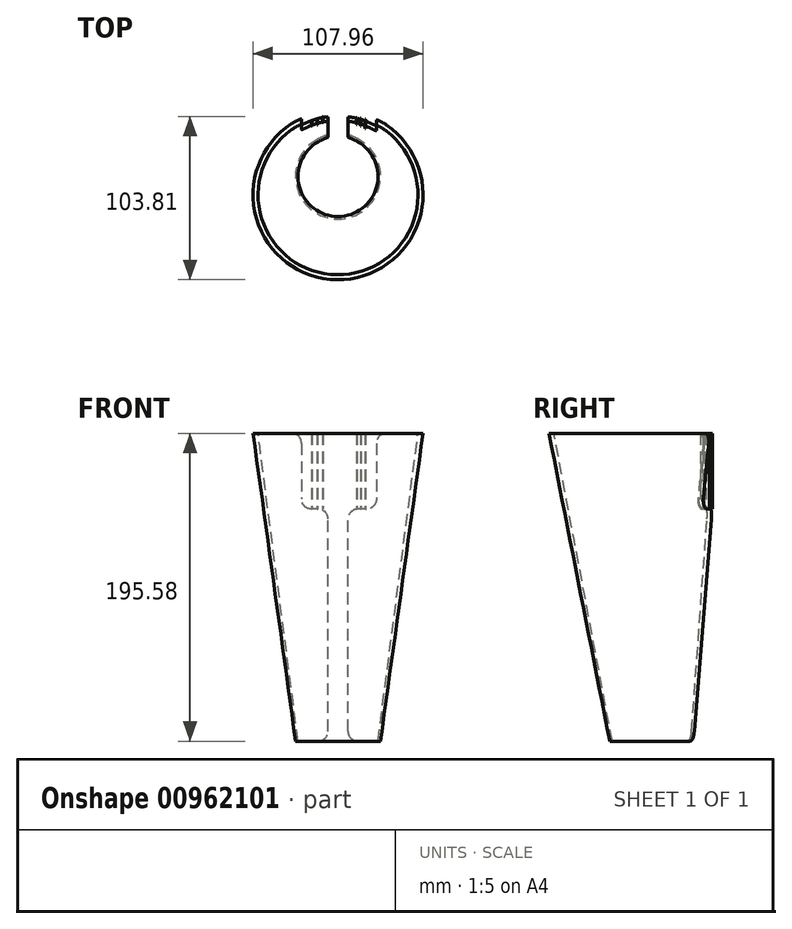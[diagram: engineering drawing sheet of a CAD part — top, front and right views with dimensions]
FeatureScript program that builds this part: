
annotation { "Feature Type Name" : "Feature", "Feature Type Description" : "" }
export const myFeature = defineFeature(function(context is Context, id is Id, definition is map)
    precondition{}
    {
        {
            var Q0;
            Q0=qCreatedBy(makeId("Top.planeOp"),FACE);
            cPlane(context, id + "F0", {"entities" : qUnion([Q0]), "cplaneType" : CPlaneType.OFFSET, "offset" : 195.58 * mm, "width" : 152.4 * mm, "height" : 152.4 * mm});
        }
        {
            var Q0;
            Q0=qCreatedBy(makeId("Top.planeOp"),FACE);
            var sketch = newSketch(context, id + "F1", { "sketchPlane" : qUnion([Q0])});
            skArc(sketch, "E0", {"start": v(-6.35, 24.6) * mm, "mid": v(0, -25.4) * mm, "end": v(6.35, 24.6) * mm});
            skArc(sketch, "E1.0", {"start": v(-6.35, 26.23) * mm, "mid": v(0, -26.99) * mm, "end": v(6.35, 26.23) * mm});
            skLineSegment(sketch, "E2", {"start": v(-6.35, 26.23) * mm, "end": v(-6.35, 24.6) * mm});
            skLineSegment(sketch, "E3", {"start": v(6.35, 26.23) * mm, "end": v(6.35, 24.6) * mm});
            skSolve(sketch);
        }
        {
            var Q0;
            Q0=qCreatedBy(id+"F0.planeOp",FACE);
            var sketch = newSketch(context, id + "F2", { "sketchPlane" : qUnion([Q0])});
            skArc(sketch, "E4", {"start": v(-6.35, 38.8) * mm, "mid": v(0, -62.4) * mm, "end": v(6.35, 38.8) * mm});
            skArc(sketch, "E5.0", {"start": v(-6.35, 42) * mm, "mid": v(0, -65.58) * mm, "end": v(6.35, 42) * mm});
            skLineSegment(sketch, "E6", {"start": v(-6.35, 42) * mm, "end": v(-6.35, 38.8) * mm});
            skLineSegment(sketch, "E7", {"start": v(6.35, 42) * mm, "end": v(6.35, 38.8) * mm});
            skSolve(sketch);
        }
        {
            var Q0;
            Q0=qSketchRegion(id+"F1",true);
            var Q1;
            Q1=qSketchRegion(id+"F2",true);
            loft(context, id + "F3", {"sheetProfilesArray" : [{ "sheetProfileEntities" : qUnion([Q0]) }, { "sheetProfileEntities" : qUnion([Q1]) }]});
        }
        {
            var Q0;
            Q0=qCreatedBy(makeId("Front.planeOp"),FACE);
            var sketch = newSketch(context, id + "F4", { "sketchPlane" : qUnion([Q0])});
            skLineSegment(sketch, "E8.bottom", {"start": v(-23.22, 213.25) * mm, "end": v(24.43, 213.25) * mm});
            skLineSegment(sketch, "E8.top", {"start": v(-23.22, 147.46) * mm, "end": v(24.43, 147.46) * mm});
            skLineSegment(sketch, "E8.left", {"start": v(-23.22, 213.25) * mm, "end": v(-23.22, 147.46) * mm});
            skLineSegment(sketch, "E8.right", {"start": v(24.43, 213.25) * mm, "end": v(24.43, 147.46) * mm});
            skSolve(sketch);
        }
        {
            var Q0;
            Q0=makeQuery(id+"F4.imprint","IMPRINT",FACE,{"disambiguationData":[TD([[makeQuery(id+"F4.imprint","IMPRINT",EDGE,{"derivedFrom":sQuery(id+"F4.wireOp",EDGE,"E8.bottom")}),-1.0]])]});
            extrude(context, id + "F5", {"entities" : qUnion([Q0]), "operationType" : NewBodyOperationType.REMOVE, "oppositeDirection" : true, "depth" : 508 * mm, "offsetDistance" : 25.4 * mm});
        }
        {
            var Q0;
            Q0=makeQuery(id+"F5.boolean.opBoolean","INTERSECT",EDGE,{"derivedFrom":[makeQuery(id+"F3.opLoft","CAP_FACE",FACE,{"disambiguationData":[OSD([makeQuery(id+"F2.imprint","IMPRINT",FACE,{"disambiguationData":[TD([[makeQuery(id+"F2.imprint","IMPRINT",EDGE,{"derivedFrom":sQuery(id+"F2.wireOp",EDGE,"E4")}),-1.0]])]})])],"isStart":true}),makeQuery(id+"F5.opExtrude","SWEPT_FACE",FACE,{"disambiguationData":[OSD([sQuery(id+"F4.wireOp",EDGE,"E8.right")])]})]});
            var Q1;
            Q1=makeQuery(id+"F5.boolean.opBoolean","COPY",EDGE,{"derivedFrom":makeQuery(id+"F5.opExtrude","SWEPT_EDGE",EDGE,{"disambiguationData":[OSD([sQuery(id+"F4.wireOp",EDGE,"E8.top"),sQuery(id+"F4.wireOp",EDGE,"E8.right")])]})});
            var Q2;
            Q2=makeQuery(id+"F5.boolean.opBoolean","INTERSECT",EDGE,{"derivedFrom":[makeQuery(id+"F3.opLoft","SWEPT_FACE",FACE,{"disambiguationData":[OSD([sQuery(id+"F1.wireOp",EDGE,"E0"),sQuery(id+"F1.wireOp",EDGE,"E1.0"),sQuery(id+"F1.wireOp",EDGE,"E3"),sQuery(id+"F2.wireOp",EDGE,"E4"),sQuery(id+"F2.wireOp",EDGE,"E5.0"),sQuery(id+"F2.wireOp",EDGE,"E7")])]}),makeQuery(id+"F5.opExtrude","SWEPT_FACE",FACE,{"disambiguationData":[OSD([sQuery(id+"F4.wireOp",EDGE,"E8.top")])]})]});
            var Q3;
            Q3=makeQuery(id+"F5.boolean.opBoolean","INTERSECT",EDGE,{"derivedFrom":[makeQuery(id+"F3.opLoft","SWEPT_FACE",FACE,{"disambiguationData":[OSD([sQuery(id+"F1.wireOp",EDGE,"E0"),sQuery(id+"F1.wireOp",EDGE,"E1.0"),sQuery(id+"F1.wireOp",EDGE,"E2"),sQuery(id+"F2.wireOp",EDGE,"E4"),sQuery(id+"F2.wireOp",EDGE,"E5.0"),sQuery(id+"F2.wireOp",EDGE,"E6")])]}),makeQuery(id+"F5.opExtrude","SWEPT_FACE",FACE,{"disambiguationData":[OSD([sQuery(id+"F4.wireOp",EDGE,"E8.top")])]})]});
            var Q4;
            Q4=makeQuery(id+"F5.boolean.opBoolean","COPY",EDGE,{"derivedFrom":makeQuery(id+"F5.opExtrude","SWEPT_EDGE",EDGE,{"disambiguationData":[OSD([sQuery(id+"F4.wireOp",EDGE,"E8.top"),sQuery(id+"F4.wireOp",EDGE,"E8.left")])]})});
            var Q5;
            Q5=makeQuery(id+"F5.boolean.opBoolean","INTERSECT",EDGE,{"derivedFrom":[makeQuery(id+"F3.opLoft","CAP_FACE",FACE,{"disambiguationData":[OSD([makeQuery(id+"F2.imprint","IMPRINT",FACE,{"disambiguationData":[TD([[makeQuery(id+"F2.imprint","IMPRINT",EDGE,{"derivedFrom":sQuery(id+"F2.wireOp",EDGE,"E4")}),-1.0]])]})])],"isStart":true}),makeQuery(id+"F5.opExtrude","SWEPT_FACE",FACE,{"disambiguationData":[OSD([sQuery(id+"F4.wireOp",EDGE,"E8.left")])]})]});
            var Q6;
            Q6=makeQuery(id+"F3.opLoft","MID_CAP_EDGE",EDGE,{"disambiguationData":[OSD([sQuery(id+"F1.wireOp",EDGE,"E0"),sQuery(id+"F1.wireOp",EDGE,"E1.0"),sQuery(id+"F1.wireOp",EDGE,"E3")])],"capPos":0.0});
            var Q7;
            Q7=makeQuery(id+"F3.opLoft","MID_CAP_EDGE",EDGE,{"disambiguationData":[OSD([sQuery(id+"F1.wireOp",EDGE,"E0"),sQuery(id+"F1.wireOp",EDGE,"E1.0"),sQuery(id+"F1.wireOp",EDGE,"E2")])],"capPos":0.0});
            fillet(context, id + "F6", {"entities" : qUnion([Q0, Q1, Q2, Q3, Q4, Q5, Q6, Q7]), "radius" : 6.35 * mm, "tangentPropagation" : true, "allowEdgeOverflow" : false});
        }
        {
            var Q0;
            {var subQ0=sQuery(id+"F2.wireOp",EDGE,"E7");var subQ1=sQuery(id+"F2.wireOp",EDGE,"E6");var subQ2=sQuery(id+"F2.wireOp",EDGE,"E4");var subQ3=sQuery(id+"F1.wireOp",EDGE,"E3");var subQ4=sQuery(id+"F1.wireOp",EDGE,"E2");var subQ5=sQuery(id+"F1.wireOp",EDGE,"E0");var subQ6=sQuery(id+"F2.wireOp",EDGE,"E5.0");var subQ7=sQuery(id+"F1.wireOp",EDGE,"E1.0");var subQ8=makeQuery(id+"F3.opLoft","SWEPT_FACE",FACE,{"disambiguationData":[OSD([subQ5,subQ7,subQ4,subQ2,subQ6,subQ1])]});var subQ9=makeQuery(id+"F3.opLoft","SWEPT_FACE",FACE,{"disambiguationData":[OSD([subQ7,subQ4,subQ3,subQ6,subQ1,subQ0])]});var subQ10=makeQuery(id+"F5.opExtrude","SWEPT_FACE",FACE,{"disambiguationData":[OSD([sQuery(id+"F4.wireOp",EDGE,"E8.top")])]});Q0=makeQuery(id+"F6.opFillet","BLEND_VERTEX",VERTEX,{"blendedFrom":[makeQuery(id+"F5.boolean.opBoolean","INTERSECT",EDGE,{"derivedFrom":[subQ8,subQ10]}),subQ9,makeQuery(id+"F5.boolean.opBoolean","COPY",FACE,{"disambiguationData":[TD([makeQuery(id+"F5.opExtrude","SWEPT_FACE",FACE,{"disambiguationData":[OSD([sQuery(id+"F4.wireOp",EDGE,"E8.left")])]})])],"derivedFrom":subQ10})],"blendedInto":[subQ9,makeQuery(id+"F5.boolean.opBoolean","COPY",FACE,{"disambiguationData":[TD([makeQuery(id+"F5.opExtrude","SWEPT_FACE",FACE,{"disambiguationData":[OSD([sQuery(id+"F4.wireOp",EDGE,"E8.left")])]})])],"derivedFrom":subQ10})]});}
            var Q1;
            {var subQ0=sQuery(id+"F2.wireOp",EDGE,"E7");var subQ1=sQuery(id+"F2.wireOp",EDGE,"E6");var subQ2=sQuery(id+"F2.wireOp",EDGE,"E4");var subQ3=sQuery(id+"F1.wireOp",EDGE,"E3");var subQ4=sQuery(id+"F1.wireOp",EDGE,"E2");var subQ5=sQuery(id+"F1.wireOp",EDGE,"E0");var subQ6=makeQuery(id+"F3.opLoft","SWEPT_FACE",FACE,{"disambiguationData":[OSD([subQ5,subQ4,subQ3,subQ2,subQ1,subQ0])]});var subQ7=sQuery(id+"F2.wireOp",EDGE,"E5.0");var subQ8=sQuery(id+"F1.wireOp",EDGE,"E1.0");var subQ9=makeQuery(id+"F3.opLoft","SWEPT_FACE",FACE,{"disambiguationData":[OSD([subQ5,subQ8,subQ4,subQ2,subQ7,subQ1])]});var subQ10=makeQuery(id+"F5.opExtrude","SWEPT_FACE",FACE,{"disambiguationData":[OSD([sQuery(id+"F4.wireOp",EDGE,"E8.top")])]});Q1=makeQuery(id+"F6.opFillet","BLEND_VERTEX",VERTEX,{"blendedFrom":[makeQuery(id+"F5.boolean.opBoolean","INTERSECT",EDGE,{"derivedFrom":[subQ9,subQ10]}),subQ6,makeQuery(id+"F5.boolean.opBoolean","COPY",FACE,{"disambiguationData":[TD([makeQuery(id+"F5.opExtrude","SWEPT_FACE",FACE,{"disambiguationData":[OSD([sQuery(id+"F4.wireOp",EDGE,"E8.left")])]})])],"derivedFrom":subQ10})],"blendedInto":[subQ6,makeQuery(id+"F5.boolean.opBoolean","COPY",FACE,{"disambiguationData":[TD([makeQuery(id+"F5.opExtrude","SWEPT_FACE",FACE,{"disambiguationData":[OSD([sQuery(id+"F4.wireOp",EDGE,"E8.left")])]})])],"derivedFrom":subQ10})]});}
            var Q2;
            {var subQ0=sQuery(id+"F2.wireOp",EDGE,"E7");var subQ1=sQuery(id+"F2.wireOp",EDGE,"E6");var subQ2=sQuery(id+"F2.wireOp",EDGE,"E4");var subQ3=sQuery(id+"F1.wireOp",EDGE,"E3");var subQ4=sQuery(id+"F1.wireOp",EDGE,"E2");var subQ5=sQuery(id+"F1.wireOp",EDGE,"E0");var subQ6=sQuery(id+"F2.wireOp",EDGE,"E5.0");var subQ7=sQuery(id+"F1.wireOp",EDGE,"E1.0");var subQ8=makeQuery(id+"F3.opLoft","SWEPT_FACE",FACE,{"disambiguationData":[OSD([subQ5,subQ7,subQ3,subQ2,subQ6,subQ0])]});var subQ9=makeQuery(id+"F3.opLoft","SWEPT_FACE",FACE,{"disambiguationData":[OSD([subQ7,subQ4,subQ3,subQ6,subQ1,subQ0])]});var subQ10=makeQuery(id+"F5.opExtrude","SWEPT_FACE",FACE,{"disambiguationData":[OSD([sQuery(id+"F4.wireOp",EDGE,"E8.top")])]});Q2=makeQuery(id+"F6.opFillet","BLEND_VERTEX",VERTEX,{"blendedFrom":[makeQuery(id+"F5.boolean.opBoolean","INTERSECT",EDGE,{"derivedFrom":[subQ8,subQ10]}),subQ9,makeQuery(id+"F5.boolean.opBoolean","COPY",FACE,{"disambiguationData":[TD([makeQuery(id+"F5.opExtrude","SWEPT_FACE",FACE,{"disambiguationData":[OSD([sQuery(id+"F4.wireOp",EDGE,"E8.right")])]})])],"derivedFrom":subQ10})],"blendedInto":[subQ9,makeQuery(id+"F5.boolean.opBoolean","COPY",FACE,{"disambiguationData":[TD([makeQuery(id+"F5.opExtrude","SWEPT_FACE",FACE,{"disambiguationData":[OSD([sQuery(id+"F4.wireOp",EDGE,"E8.right")])]})])],"derivedFrom":subQ10})]});}
            cPlane(context, id + "F7", {"entities" : qUnion([Q0, Q1, Q2]), "cplaneType" : CPlaneType.THREE_POINT, "offset" : 25.4 * mm, "width" : 152.4 * mm, "height" : 152.4 * mm});
        }
        {
            var Q0;
            Q0=qCreatedBy(id+"F7.planeOp",FACE);
            var sketch = newSketch(context, id + "F8", { "sketchPlane" : qUnion([Q0])});
            skLineSegment(sketch, "E9.bottom", {"start": v(-16.94, -35.6) * mm, "end": v(-16.66, -35.6) * mm});
            skLineSegment(sketch, "E9.top", {"start": v(-16.94, -32.12) * mm, "end": v(-16.66, -32.12) * mm});
            skLineSegment(sketch, "E9.left", {"start": v(-16.94, -35.6) * mm, "end": v(-16.94, -32.12) * mm});
            skLineSegment(sketch, "E9.right", {"start": v(-16.66, -35.6) * mm, "end": v(-16.66, -32.12) * mm});
            skLineSegment(sketch, "E10.bottom", {"start": v(-13.28, -36.94) * mm, "end": v(-12.87, -36.94) * mm});
            skLineSegment(sketch, "E10.top", {"start": v(-13.28, -32.7) * mm, "end": v(-12.87, -32.7) * mm});
            skLineSegment(sketch, "E10.left", {"start": v(-13.28, -36.94) * mm, "end": v(-13.28, -32.7) * mm});
            skLineSegment(sketch, "E10.right", {"start": v(-12.87, -36.94) * mm, "end": v(-12.87, -32.7) * mm});
            skLineSegment(sketch, "E11.bottom", {"start": v(-9.87, -38.23) * mm, "end": v(-9.55, -38.23) * mm});
            skLineSegment(sketch, "E11.top", {"start": v(-9.87, -34.19) * mm, "end": v(-9.55, -34.19) * mm});
            skLineSegment(sketch, "E11.left", {"start": v(-9.87, -38.23) * mm, "end": v(-9.87, -34.19) * mm});
            skLineSegment(sketch, "E11.right", {"start": v(-9.55, -38.23) * mm, "end": v(-9.55, -34.19) * mm});
            skLineSegment(sketch, "E12.bottom", {"start": v(11.7, -37.57) * mm, "end": v(11.97, -37.57) * mm});
            skLineSegment(sketch, "E12.top", {"start": v(11.7, -32.86) * mm, "end": v(11.97, -32.86) * mm});
            skLineSegment(sketch, "E12.left", {"start": v(11.7, -37.57) * mm, "end": v(11.7, -32.86) * mm});
            skLineSegment(sketch, "E12.right", {"start": v(11.97, -37.57) * mm, "end": v(11.97, -32.86) * mm});
            skLineSegment(sketch, "E13.bottom", {"start": v(14.36, -37.03) * mm, "end": v(14.65, -37.03) * mm});
            skLineSegment(sketch, "E13.top", {"start": v(14.36, -32.18) * mm, "end": v(14.65, -32.18) * mm});
            skLineSegment(sketch, "E13.left", {"start": v(14.36, -37.03) * mm, "end": v(14.36, -32.18) * mm});
            skLineSegment(sketch, "E13.right", {"start": v(14.65, -37.03) * mm, "end": v(14.65, -32.18) * mm});
            skLineSegment(sketch, "E14.bottom", {"start": v(17.25, -36.46) * mm, "end": v(17.53, -36.46) * mm});
            skLineSegment(sketch, "E14.top", {"start": v(17.25, -30.61) * mm, "end": v(17.53, -30.61) * mm});
            skLineSegment(sketch, "E14.left", {"start": v(17.25, -36.46) * mm, "end": v(17.25, -30.61) * mm});
            skLineSegment(sketch, "E14.right", {"start": v(17.53, -36.46) * mm, "end": v(17.53, -30.61) * mm});
            skSolve(sketch);
        }
        {
            var Q0;
            Q0 = qSketchRegion(id + "F8", true);
            var Q1;
            Q1=qCreatedBy(makeId("Top.planeOp"),FACE);
            extrude(context, id + "F9", {"entities" : qUnion([Q0]), "operationType" : NewBodyOperationType.ADD, "oppositeDirection" : true, "depth" : 48.03 * mm, "endBoundEntityFace" : qUnion([Q1]), "offsetDistance" : 25.4 * mm});
        }
    });
